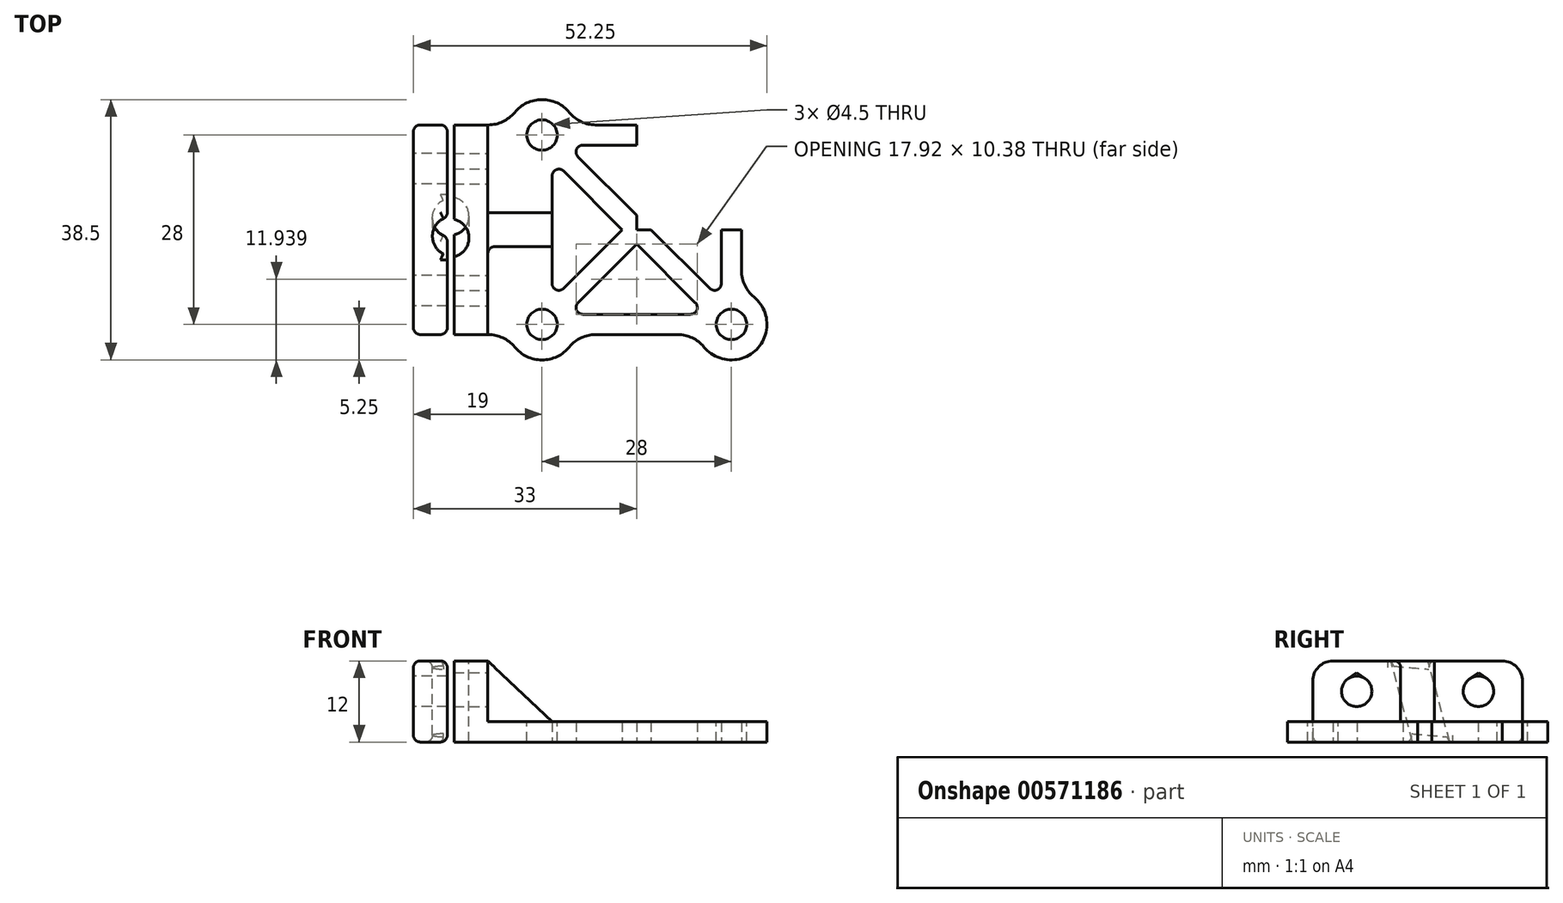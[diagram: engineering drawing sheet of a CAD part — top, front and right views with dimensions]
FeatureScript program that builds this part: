
annotation { "Feature Type Name" : "Feature", "Feature Type Description" : "" }
export const myFeature = defineFeature(function(context is Context, id is Id, definition is map)
    precondition{}
    {
        {
            var Q0;
            Q0=qCreatedBy(makeId("Top.planeOp"),FACE);
            var sketch = newSketch(context, id + "F0", { "sketchPlane" : qUnion([Q0])});
            skCircle(sketch, "E0", {"center": v(-27.5, 0) * mm, "radius": 2.5 * mm});
            skSolve(sketch);
        }
        {
            var Q0;
            Q0=makeQuery(id+"F0.imprint","IMPRINT",FACE,{"disambiguationData":[TD([[makeQuery(id+"F0.imprint","IMPRINT",EDGE,{"derivedFrom":sQuery(id+"F0.wireOp",EDGE,"E0")}),1.0]])]});
            extrude(context, id + "F1", {"entities" : qUnion([Q0]), "endBound" : BoundingType.SYMMETRIC, "depth" : 35 * mm, "offsetDistance" : 25 * mm});
        }
        {
            var Q0;
            Q0=qCreatedBy(makeId("Front.planeOp"),FACE);
            var sketch = newSketch(context, id + "F2", { "sketchPlane" : qUnion([Q0])});
            skLineSegment(sketch, "E1", {"start": v(0, 7.5) * mm, "end": v(-27.5, 7.5) * mm, "construction": true});
            skSolve(sketch);
        }
        {
            var Q0;
            Q0=makeQuery(id+"F1.opExtrude","SWEPT_BODY",BODY,{"disambiguationData":[OSD([sQuery(id+"F0.wireOp",EDGE,"E0")])]});
            var Q1;
            Q1=sQuery(id+"F2.wireOp",EDGE,"E1");
            transform(context, id + "F3", {"entities" : qUnion([Q0]), "transformType" : TransformType.ROTATION, "transformAxis" : qUnion([Q1]), "angle" : 15 * degree, "oppositeDirection" : true, "makeCopy" : false});
        }
        {
            var Q0;
            Q0=qCreatedBy(makeId("Top.planeOp"),FACE);
            var sketch = newSketch(context, id + "F4", { "sketchPlane" : qUnion([Q0])});
            skArc(sketch, "E2", {"start": v(-15.5, -8.97) * mm, "mid": v(-17.71, -17.71) * mm, "end": v(-8.97, -15.5) * mm});
            skCircle(sketch, "E3", {"center": v(-14, -14) * mm, "radius": 2.25 * mm, "construction": true});
            skLineSegment(sketch, "E4", {"start": v(-14, -14) * mm, "end": v(0, -14) * mm, "construction": true});
            skLineSegment(sketch, "E5", {"start": v(0, 0) * mm, "end": v(-14, -14) * mm, "construction": true});
            skLineSegment(sketch, "E6", {"start": v(-14, 0) * mm, "end": v(-14, -14) * mm, "construction": true});
            skLineSegment(sketch, "E7", {"start": v(-8.97, -15.5) * mm, "end": v(0, -15.5) * mm});
            skLineSegment(sketch, "E8", {"start": v(0, -15.5) * mm, "end": v(0, -14) * mm});
            skLineSegment(sketch, "E9", {"start": v(0, -12.5) * mm, "end": v(-7.96, -12.5) * mm});
            skLineSegment(sketch, "E10", {"start": v(-15.5, -8.97) * mm, "end": v(-15.5, 0) * mm});
            skLineSegment(sketch, "E11", {"start": v(-15.5, 0) * mm, "end": v(-14, 0) * mm});
            skLineSegment(sketch, "E12", {"start": v(-10.8, -8.67) * mm, "end": v(-2.12, 0) * mm});
            skLineSegment(sketch, "E13", {"start": v(0, -2.12) * mm, "end": v(-8.67, -10.8) * mm});
            skLineSegment(sketch, "E14", {"start": v(-14, 0) * mm, "end": v(-12.5, 0) * mm});
            skLineSegment(sketch, "E15", {"start": v(-12.5, 0) * mm, "end": v(-12.5, -7.96) * mm});
            skLineSegment(sketch, "E16", {"start": v(0, -12.5) * mm, "end": v(0, -14) * mm});
            skArc(sketch, "E17", {"start": v(-12.5, -7.96) * mm, "mid": v(-11.88, -8.89) * mm, "end": v(-10.8, -8.67) * mm});
            skArc(sketch, "E18", {"start": v(-8.67, -10.8) * mm, "mid": v(-8.89, -11.88) * mm, "end": v(-7.96, -12.5) * mm});
            skLineSegment(sketch, "E19", {"start": v(-2.12, 0) * mm, "end": v(0, 0) * mm});
            skLineSegment(sketch, "E20", {"start": v(0, 0) * mm, "end": v(0, -2.12) * mm});
            skLineSegment(sketch, "E21", {"start": v(-2.12, 0) * mm, "end": v(-1.06, -1.06) * mm, "construction": true});
            skLineSegment(sketch, "E22", {"start": v(-1.06, -1.06) * mm, "end": v(0, -2.12) * mm, "construction": true});
            skSolve(sketch);
        }
        {
            var Q0;
            Q0 = qSketchRegion(id + "F4", true);
            extrude(context, id + "F5", {"entities" : qUnion([Q0]), "depth" : 3 * mm, "offsetDistance" : 25 * mm});
        }
        {
            var Q0;
            Q0=makeQuery(id+"F5.opExtrude","CAP_FACE",FACE,{"disambiguationData":[OSD([sQuery(id+"F4.wireOp",EDGE,"E2"),sQuery(id+"F4.wireOp",EDGE,"E7"),sQuery(id+"F4.wireOp",EDGE,"E8"),sQuery(id+"F4.wireOp",EDGE,"E9"),sQuery(id+"F4.wireOp",EDGE,"E10"),sQuery(id+"F4.wireOp",EDGE,"E11"),sQuery(id+"F4.wireOp",EDGE,"E12"),sQuery(id+"F4.wireOp",EDGE,"Kl6RHnXf-nioG-wzmg-PsDO-Y8z6quR7Twf4"),sQuery(id+"F4.wireOp",EDGE,"E13"),sQuery(id+"F4.wireOp",EDGE,"E14"),sQuery(id+"F4.wireOp",EDGE,"E15"),sQuery(id+"F4.wireOp",EDGE,"vt1vT131-rDiG-MxEs-hZJZ-qJtVu3JIf4gR"),sQuery(id+"F4.wireOp",EDGE,"E16"),sQuery(id+"F4.wireOp",EDGE,"E17"),sQuery(id+"F4.wireOp",EDGE,"E18")])],"isStart":false});
            var sketch = newSketch(context, id + "F6", { "sketchPlane" : qUnion([Q0])});
            skCircle(sketch, "E23", {"center": v(-14, -14) * mm, "radius": 2.25 * mm});
            skSolve(sketch);
        }
        {
            var Q0;
            Q0 = qSketchRegion(id + "F6", true);
            var Q1;
            Q1=makeQuery(id+"F5.opExtrude","CAP_FACE",FACE,{"disambiguationData":[OSD([sQuery(id+"F4.wireOp",EDGE,"E2"),sQuery(id+"F4.wireOp",EDGE,"E7"),sQuery(id+"F4.wireOp",EDGE,"E8"),sQuery(id+"F4.wireOp",EDGE,"E9"),sQuery(id+"F4.wireOp",EDGE,"E10"),sQuery(id+"F4.wireOp",EDGE,"E11"),sQuery(id+"F4.wireOp",EDGE,"E12"),sQuery(id+"F4.wireOp",EDGE,"Kl6RHnXf-nioG-wzmg-PsDO-Y8z6quR7Twf4"),sQuery(id+"F4.wireOp",EDGE,"E13"),sQuery(id+"F4.wireOp",EDGE,"E14"),sQuery(id+"F4.wireOp",EDGE,"E15"),sQuery(id+"F4.wireOp",EDGE,"vt1vT131-rDiG-MxEs-hZJZ-qJtVu3JIf4gR"),sQuery(id+"F4.wireOp",EDGE,"E16"),sQuery(id+"F4.wireOp",EDGE,"E17"),sQuery(id+"F4.wireOp",EDGE,"E18")])],"isStart":true});
            extrude(context, id + "F7", {"entities" : qUnion([Q0]), "operationType" : NewBodyOperationType.REMOVE, "endBound" : BoundingType.UP_TO_SURFACE, "oppositeDirection" : true, "depth" : 25 * mm, "endBoundEntityFace" : qUnion([Q1]), "offsetDistance" : 25 * mm});
        }
        {
            var Q0;
            Q0=makeQuery(id+"F5.opExtrude","SWEPT_BODY",BODY,{"disambiguationData":[OSD([sQuery(id+"F4.wireOp",EDGE,"E2"),sQuery(id+"F4.wireOp",EDGE,"E7"),sQuery(id+"F4.wireOp",EDGE,"E8"),sQuery(id+"F4.wireOp",EDGE,"E9"),sQuery(id+"F4.wireOp",EDGE,"E10"),sQuery(id+"F4.wireOp",EDGE,"E11"),sQuery(id+"F4.wireOp",EDGE,"E12"),sQuery(id+"F4.wireOp",EDGE,"Kl6RHnXf-nioG-wzmg-PsDO-Y8z6quR7Twf4"),sQuery(id+"F4.wireOp",EDGE,"E13"),sQuery(id+"F4.wireOp",EDGE,"E14"),sQuery(id+"F4.wireOp",EDGE,"E15"),sQuery(id+"F4.wireOp",EDGE,"vt1vT131-rDiG-MxEs-hZJZ-qJtVu3JIf4gR"),sQuery(id+"F4.wireOp",EDGE,"E16"),sQuery(id+"F4.wireOp",EDGE,"E17"),sQuery(id+"F4.wireOp",EDGE,"E18")])]});
            var Q1;
            Q1=qCreatedBy(makeId("Right.planeOp"),FACE);
            mirror(context, id + "F8", {"operationType" : NewBodyOperationType.ADD, "entities" : qUnion([Q0]), "mirrorPlane" : qUnion([Q1])});
        }
        {
            var Q0;
            Q0=makeQuery(id+"F5.opExtrude","SWEPT_BODY",BODY,{"disambiguationData":[OSD([sQuery(id+"F4.wireOp",EDGE,"E2"),sQuery(id+"F4.wireOp",EDGE,"E7"),sQuery(id+"F4.wireOp",EDGE,"E8"),sQuery(id+"F4.wireOp",EDGE,"E9"),sQuery(id+"F4.wireOp",EDGE,"E10"),sQuery(id+"F4.wireOp",EDGE,"E11"),sQuery(id+"F4.wireOp",EDGE,"E12"),sQuery(id+"F4.wireOp",EDGE,"Kl6RHnXf-nioG-wzmg-PsDO-Y8z6quR7Twf4"),sQuery(id+"F4.wireOp",EDGE,"E13"),sQuery(id+"F4.wireOp",EDGE,"E14"),sQuery(id+"F4.wireOp",EDGE,"E15"),sQuery(id+"F4.wireOp",EDGE,"vt1vT131-rDiG-MxEs-hZJZ-qJtVu3JIf4gR"),sQuery(id+"F4.wireOp",EDGE,"E16"),sQuery(id+"F4.wireOp",EDGE,"E17"),sQuery(id+"F4.wireOp",EDGE,"E18")])]});
            var Q1;
            Q1=qCreatedBy(makeId("Front.planeOp"),FACE);
            mirror(context, id + "F9", {"operationType" : NewBodyOperationType.ADD, "entities" : qUnion([Q0]), "mirrorPlane" : qUnion([Q1])});
        }
        {
            var Q0;
            Q0=qCreatedBy(makeId("Top.planeOp"),FACE);
            var sketch = newSketch(context, id + "F10", { "sketchPlane" : qUnion([Q0])});
            skLineSegment(sketch, "E24", {"start": v(-22, 0) * mm, "end": v(-22, -15.5) * mm});
            skLineSegment(sketch, "E25", {"start": v(-22, -15.5) * mm, "end": v(-33, -15.5) * mm});
            skLineSegment(sketch, "E26", {"start": v(-33, -15.5) * mm, "end": v(-33, 0) * mm});
            skLineSegment(sketch, "E27.MirrorCS", {"start": v(-22, 0) * mm, "end": v(-22, 15.5) * mm});
            skLineSegment(sketch, "E28.MirrorCS", {"start": v(-22, 15.5) * mm, "end": v(-33, 15.5) * mm});
            skLineSegment(sketch, "E29.MirrorCS", {"start": v(-33, 15.5) * mm, "end": v(-33, 0) * mm});
            skSolve(sketch);
        }
        {
            var Q0;
            Q0 = qSketchRegion(id + "F10", true);
            extrude(context, id + "F11", {"entities" : qUnion([Q0]), "operationType" : NewBodyOperationType.ADD, "depth" : 12 * mm, "offsetDistance" : 25 * mm});
        }
        {
            var Q0;
            Q0=qCreatedBy(makeId("Top.planeOp"),FACE);
            var sketch = newSketch(context, id + "F12", { "sketchPlane" : qUnion([Q0])});
            skLineSegment(sketch, "E30", {"start": v(-15.68, -15.5) * mm, "end": v(-22, -15.5) * mm});
            skLineSegment(sketch, "E31", {"start": v(-14, 0) * mm, "end": v(-14, -11.75) * mm});
            skArc(sketch, "E32", {"start": v(-14, -11.75) * mm, "mid": v(-16.05, -13.08) * mm, "end": v(-15.68, -15.5) * mm});
            skLineSegment(sketch, "E33", {"start": v(-22, 0) * mm, "end": v(-22, -15.5) * mm});
            skLineSegment(sketch, "E34.MirrorCS", {"start": v(-14, 0) * mm, "end": v(-14, 11.75) * mm});
            skArc(sketch, "E35.MirrorCS", {"start": v(-14, 11.75) * mm, "mid": v(-16.05, 13.08) * mm, "end": v(-15.68, 15.5) * mm});
            skLineSegment(sketch, "E36.MirrorCS", {"start": v(-15.68, 15.5) * mm, "end": v(-22, 15.5) * mm});
            skLineSegment(sketch, "E37.MirrorCS", {"start": v(-22, 0) * mm, "end": v(-22, 15.5) * mm});
            skSolve(sketch);
        }
        {
            var Q0;
            Q0 = qSketchRegion(id + "F12", true);
            var Q1;
            {var subQ0=makeQuery(id+"F5.opExtrude","CAP_FACE",FACE,{"disambiguationData":[OSD([sQuery(id+"F4.wireOp",EDGE,"E2"),sQuery(id+"F4.wireOp",EDGE,"E7"),sQuery(id+"F4.wireOp",EDGE,"E8"),sQuery(id+"F4.wireOp",EDGE,"E9"),sQuery(id+"F4.wireOp",EDGE,"E10"),sQuery(id+"F4.wireOp",EDGE,"E11"),sQuery(id+"F4.wireOp",EDGE,"E12"),sQuery(id+"F4.wireOp",EDGE,"E13"),sQuery(id+"F4.wireOp",EDGE,"E14"),sQuery(id+"F4.wireOp",EDGE,"E15"),sQuery(id+"F4.wireOp",EDGE,"E16"),sQuery(id+"F4.wireOp",EDGE,"E17"),sQuery(id+"F4.wireOp",EDGE,"E18"),sQuery(id+"F4.wireOp",EDGE,"E19"),sQuery(id+"F4.wireOp",EDGE,"E20")])],"isStart":false});var subQ1=makeQuery(id+"F8.boolean.opBoolean","MERGE",FACE,{"derivedFrom":[subQ0,makeQuery(id+"F8.opPattern","COPY",FACE,{"derivedFrom":subQ0,"instanceName":"1"})]});Q1=makeQuery(id+"F9.boolean.opBoolean","MERGE",FACE,{"derivedFrom":[subQ1,makeQuery(id+"F9.opPattern","COPY",FACE,{"derivedFrom":subQ1,"instanceName":"1"})]});}
            extrude(context, id + "F13", {"entities" : qUnion([Q0]), "operationType" : NewBodyOperationType.ADD, "endBound" : BoundingType.UP_TO_SURFACE, "depth" : 25 * mm, "endBoundEntityFace" : qUnion([Q1]), "offsetDistance" : 25 * mm});
        }
        {
            var Q0;
            Q0=qCreatedBy(makeId("Front.planeOp"),FACE);
            var sketch = newSketch(context, id + "F14", { "sketchPlane" : qUnion([Q0])});
            skLineSegment(sketch, "E38", {"start": v(-22, 12) * mm, "end": v(-12.5, 3) * mm});
            skLineSegment(sketch, "E39", {"start": v(-22, 3) * mm, "end": v(-22, 12) * mm});
            skLineSegment(sketch, "E40", {"start": v(-12.5, 3) * mm, "end": v(-22, 3) * mm});
            skSolve(sketch);
        }
        {
            var Q0;
            Q0 = qSketchRegion(id + "F14", true);
            var Q1;
            Q1=makeQuery(id+"F13.opExtrude","SWEPT_FACE",FACE,{"disambiguationData":[OSD([sQuery(id+"F12.wireOp",EDGE,"puVTzyak-XMDq-GeyV-AaeZ-wzUpr93Q762x")])]});
            var Q2;
            Q2=makeQuery(id+"F13.opExtrude","SWEPT_FACE",FACE,{"disambiguationData":[OSD([sQuery(id+"F12.wireOp",EDGE,"d726f810-fd56-4b56-9927-8afe40f47e5f0.MirrorCS")])]});
            extrude(context, id + "F15", {"entities" : qUnion([Q0]), "operationType" : NewBodyOperationType.ADD, "endBound" : BoundingType.SYMMETRIC, "depth" : 5 * mm, "endBoundEntityFace" : qUnion([Q1]), "offsetDistance" : 25 * mm, "hasSecondDirection" : true, "secondDirectionBound" : SecondDirectionBoundingType.UP_TO_SURFACE, "secondDirectionOppositeDirection" : true, "secondDirectionDepth" : 25 * mm, "secondDirectionBoundEntityFace" : qUnion([Q2])});
        }
        {
            var Q0;
            Q0=makeQuery(id+"F1.opExtrude","CAP_FACE",FACE,{"disambiguationData":[OSD([sQuery(id+"F0.wireOp",EDGE,"E0")])],"isStart":false});
            var sketch = newSketch(context, id + "F16", { "sketchPlane" : qUnion([Q0])});
            skArc(sketch, "E41", {"start": v(-27, -0.71) * mm, "mid": v(-24.8, 1.94) * mm, "end": v(-27, 4.6) * mm});
            skLineSegment(sketch, "E42.top", {"start": v(-28, -23.06) * mm, "end": v(-27, -23.06) * mm});
            skLineSegment(sketch, "E42.left", {"start": v(-28, -0.71) * mm, "end": v(-28, -23.06) * mm});
            skLineSegment(sketch, "E42.right", {"start": v(-27, -0.71) * mm, "end": v(-27, -23.06) * mm});
            skLineSegment(sketch, "E43.MirrorCS", {"start": v(-28, 4.6) * mm, "end": v(-28, 26.94) * mm});
            skLineSegment(sketch, "E44.MirrorCS", {"start": v(-28, 26.94) * mm, "end": v(-27, 26.94) * mm});
            skLineSegment(sketch, "E45.MirrorCS", {"start": v(-27, 4.6) * mm, "end": v(-27, 26.94) * mm});
            skArc(sketch, "E46.trimOffspring", {"start": v(-28, 4.6) * mm, "mid": v(-30.2, 1.94) * mm, "end": v(-28, -0.71) * mm});
            skSolve(sketch);
        }
        {
            var Q0;
            Q0 = qSketchRegion(id + "F16", true);
            extrude(context, id + "F17", {"entities" : qUnion([Q0]), "operationType" : NewBodyOperationType.REMOVE, "oppositeDirection" : true, "depth" : 50 * mm, "offsetDistance" : 25 * mm});
        }
        {
            var Q0;
            {var subQ33=sQuery(id+"F10.wireOp",EDGE,"E27.MirrorCS");var subQ35=sQuery(id+"F10.wireOp",EDGE,"E25");var subQ36=sQuery(id+"F10.wireOp",EDGE,"E24");Q0=makeQuery(id+"F15.boolean.opBoolean","SPLIT",FACE,{"disambiguationData":[TD([makeQuery(id+"F11.opExtrude","SWEPT_FACE",FACE,{"disambiguationData":[OSD([subQ35])]})])],"derivedFrom":makeQuery(id+"F11.opExtrude","SWEPT_FACE",FACE,{"disambiguationData":[OSD([subQ36,subQ33])]})});}
            var sketch = newSketch(context, id + "F18", { "sketchPlane" : qUnion([Q0])});
            skLineSegment(sketch, "E47", {"start": v(-15.5, 3) * mm, "end": v(-2.5, 12) * mm, "construction": true});
            skLineSegment(sketch, "E48", {"start": v(-15.5, 12) * mm, "end": v(-2.5, 3) * mm, "construction": true});
            skArc(sketch, "E49", {"start": v(-10.3, 9.34) * mm, "mid": v(-9, 5.25) * mm, "end": v(-7.7, 9.34) * mm});
            skLineSegment(sketch, "E50", {"start": v(-10.3, 9.34) * mm, "end": v(-9, 10.25) * mm});
            skLineSegment(sketch, "E51", {"start": v(-9, 10.25) * mm, "end": v(-7.7, 9.34) * mm});
            skLineSegment(sketch, "E52.MirrorCS", {"start": v(9, 10.25) * mm, "end": v(7.7, 9.34) * mm});
            skArc(sketch, "E53.MirrorCS", {"start": v(10.3, 9.34) * mm, "mid": v(9, 5.25) * mm, "end": v(7.7, 9.34) * mm});
            skLineSegment(sketch, "E54.MirrorCS", {"start": v(10.3, 9.34) * mm, "end": v(9, 10.25) * mm});
            skSolve(sketch);
        }
        {
            var Q0;
            Q0 = qSketchRegion(id + "F18", true);
            var Q1;
            Q1=makeQuery(id+"F17.boolean.opBoolean","COPY",FACE,{"derivedFrom":makeQuery(id+"F17.opExtrude","SWEPT_FACE",FACE,{"disambiguationData":[OSD([sQuery(id+"F16.wireOp",EDGE,"E42.right")])]})});
            extrude(context, id + "F19", {"entities" : qUnion([Q0]), "operationType" : NewBodyOperationType.REMOVE, "endBound" : BoundingType.UP_TO_SURFACE, "oppositeDirection" : true, "depth" : 25 * mm, "endBoundEntityFace" : qUnion([Q1]), "offsetDistance" : 25 * mm});
        }
        {
            var Q0;
            Q0=makeQuery(id+"F11.opExtrude","SWEPT_FACE",FACE,{"disambiguationData":[OSD([sQuery(id+"F10.wireOp",EDGE,"E26"),sQuery(id+"F10.wireOp",EDGE,"E29.MirrorCS")])]});
            var sketch = newSketch(context, id + "F20", { "sketchPlane" : qUnion([Q0])});
            skCircle(sketch, "E55", {"center": v(9, 7.5) * mm, "radius": 2.25 * mm});
            skCircle(sketch, "E56.MirrorC", {"center": v(-9, 7.5) * mm, "radius": 2.25 * mm});
            skSolve(sketch);
        }
        {
            var Q0;
            Q0 = qSketchRegion(id + "F20", true);
            var Q1;
            Q1=makeQuery(id+"F17.boolean.opBoolean","COPY",FACE,{"derivedFrom":makeQuery(id+"F17.opExtrude","SWEPT_FACE",FACE,{"disambiguationData":[OSD([sQuery(id+"F16.wireOp",EDGE,"E42.left")])]})});
            extrude(context, id + "F21", {"entities" : qUnion([Q0]), "operationType" : NewBodyOperationType.REMOVE, "endBound" : BoundingType.UP_TO_SURFACE, "oppositeDirection" : true, "depth" : 25 * mm, "endBoundEntityFace" : qUnion([Q1]), "offsetDistance" : 25 * mm});
        }
        {
            var Q0;
            Q0=makeQuery(id+"F9.opPattern","COPY",EDGE,{"derivedFrom":makeQuery(id+"F8.opPattern","COPY",EDGE,{"derivedFrom":makeQuery(id+"F5.opExtrude","SWEPT_EDGE",EDGE,{"disambiguationData":[OSD([sQuery(id+"F4.wireOp",EDGE,"E2"),sQuery(id+"F4.wireOp",EDGE,"E7")])]}),"instanceName":"1"}),"instanceName":"1"});
            var Q1;
            Q1=makeQuery(id+"F9.opPattern","COPY",EDGE,{"derivedFrom":makeQuery(id+"F5.opExtrude","SWEPT_EDGE",EDGE,{"disambiguationData":[OSD([sQuery(id+"F4.wireOp",EDGE,"E2"),sQuery(id+"F4.wireOp",EDGE,"E7")])]}),"instanceName":"1"});
            var Q2;
            Q2=makeQuery(id+"F9.opPattern","COPY",EDGE,{"derivedFrom":makeQuery(id+"F5.opExtrude","SWEPT_EDGE",EDGE,{"disambiguationData":[OSD([sQuery(id+"F4.wireOp",EDGE,"E2"),sQuery(id+"F4.wireOp",EDGE,"E10")])]}),"instanceName":"1"});
            var Q3;
            Q3=makeQuery(id+"F5.opExtrude","SWEPT_EDGE",EDGE,{"disambiguationData":[OSD([sQuery(id+"F4.wireOp",EDGE,"E2"),sQuery(id+"F4.wireOp",EDGE,"E10")])]});
            var Q4;
            Q4=makeQuery(id+"F5.opExtrude","SWEPT_EDGE",EDGE,{"disambiguationData":[OSD([sQuery(id+"F4.wireOp",EDGE,"E2"),sQuery(id+"F4.wireOp",EDGE,"E7")])]});
            var Q5;
            Q5=makeQuery(id+"F8.opPattern","COPY",EDGE,{"derivedFrom":makeQuery(id+"F5.opExtrude","SWEPT_EDGE",EDGE,{"disambiguationData":[OSD([sQuery(id+"F4.wireOp",EDGE,"E2"),sQuery(id+"F4.wireOp",EDGE,"E7")])]}),"instanceName":"1"});
            var Q6;
            Q6=makeQuery(id+"F8.opPattern","COPY",EDGE,{"derivedFrom":makeQuery(id+"F5.opExtrude","SWEPT_EDGE",EDGE,{"disambiguationData":[OSD([sQuery(id+"F4.wireOp",EDGE,"E2"),sQuery(id+"F4.wireOp",EDGE,"E10")])]}),"instanceName":"1"});
            var Q7;
            Q7=makeQuery(id+"F9.opPattern","COPY",EDGE,{"derivedFrom":makeQuery(id+"F8.opPattern","COPY",EDGE,{"derivedFrom":makeQuery(id+"F5.opExtrude","SWEPT_EDGE",EDGE,{"disambiguationData":[OSD([sQuery(id+"F4.wireOp",EDGE,"E2"),sQuery(id+"F4.wireOp",EDGE,"E10")])]}),"instanceName":"1"}),"instanceName":"1"});
            var Q8;
            Q8=makeQuery(id+"F13.boolean.opBoolean","INTERSECT",EDGE,{"derivedFrom":[makeQuery(id+"F5.opExtrude","SWEPT_FACE",FACE,{"disambiguationData":[OSD([sQuery(id+"F4.wireOp",EDGE,"E2")])]}),makeQuery(id+"F13.opExtrude","SWEPT_FACE",FACE,{"disambiguationData":[OSD([sQuery(id+"F12.wireOp",EDGE,"E30")])]})]});
            var Q9;
            Q9=makeQuery(id+"F13.boolean.opBoolean","INTERSECT",EDGE,{"derivedFrom":[makeQuery(id+"F9.opPattern","COPY",FACE,{"derivedFrom":makeQuery(id+"F5.opExtrude","SWEPT_FACE",FACE,{"disambiguationData":[OSD([sQuery(id+"F4.wireOp",EDGE,"E2")])]}),"instanceName":"1"}),makeQuery(id+"F13.opExtrude","SWEPT_FACE",FACE,{"disambiguationData":[OSD([sQuery(id+"F12.wireOp",EDGE,"E36.MirrorCS")])]})]});
            fillet(context, id + "F22", {"entities" : qUnion([Q0, Q1, Q2, Q3, Q4, Q5, Q6, Q7, Q8, Q9]), "radius" : 5 * mm, "tangentPropagation" : true, "allowEdgeOverflow" : false});
        }
        {
            var Q0;
            Q0=makeQuery(id+"F15.opExtrude","CAP_EDGE",EDGE,{"disambiguationData":[OSD([sQuery(id+"F14.wireOp",EDGE,"E39")])],"isStart":false});
            var Q1;
            Q1=makeQuery(id+"F15.opExtrude","CAP_EDGE",EDGE,{"disambiguationData":[OSD([sQuery(id+"F14.wireOp",EDGE,"E40")])],"isStart":false});
            var Q2;
            {var subQ4=sQuery(id+"F12.wireOp",EDGE,"E37.MirrorCS");var subQ5=sQuery(id+"F12.wireOp",EDGE,"E33");Q2=makeQuery(id+"F15.boolean.opBoolean","SPLIT",EDGE,{"disambiguationData":[TD([makeQuery(id+"F11.opExtrude","SWEPT_FACE",FACE,{"disambiguationData":[OSD([sQuery(id+"F10.wireOp",EDGE,"E25")])]})])],"derivedFrom":makeQuery(id+"F13.opExtrude","CAP_EDGE",EDGE,{"disambiguationData":[OSD([subQ5,subQ4])],"isStart":false})});}
            var Q3;
            Q3=makeQuery(id+"F15.opExtrude","CAP_EDGE",EDGE,{"disambiguationData":[OSD([sQuery(id+"F14.wireOp",EDGE,"E40")])],"isStart":true});
            var Q4;
            Q4=makeQuery(id+"F15.opExtrude","CAP_EDGE",EDGE,{"disambiguationData":[OSD([sQuery(id+"F14.wireOp",EDGE,"E39")])],"isStart":true});
            var Q5;
            {var subQ3=sQuery(id+"F12.wireOp",EDGE,"E37.MirrorCS");var subQ5=sQuery(id+"F12.wireOp",EDGE,"E33");Q5=makeQuery(id+"F15.boolean.opBoolean","SPLIT",EDGE,{"disambiguationData":[TD([makeQuery(id+"F11.opExtrude","SWEPT_FACE",FACE,{"disambiguationData":[OSD([sQuery(id+"F10.wireOp",EDGE,"E28.MirrorCS")])]})])],"derivedFrom":makeQuery(id+"F13.opExtrude","CAP_EDGE",EDGE,{"disambiguationData":[OSD([subQ5,subQ3])],"isStart":false})});}
            fillet(context, id + "F23", {"entities" : qUnion([Q0, Q1, Q2, Q3, Q4, Q5]), "radius" : 1 * mm, "tangentPropagation" : true, "allowEdgeOverflow" : false});
        }
        {
            var Q0;
            {var subQ0=sQuery(id+"F10.wireOp",EDGE,"E25");Q0=makeQuery(id+"F17.boolean.opBoolean","SPLIT",EDGE,{"disambiguationData":[TD([makeQuery(id+"F17.opExtrude","SWEPT_FACE",FACE,{"disambiguationData":[OSD([sQuery(id+"F16.wireOp",EDGE,"E42.right")])]})])],"derivedFrom":makeQuery(id+"F11.opExtrude","CAP_EDGE",EDGE,{"disambiguationData":[OSD([subQ0])],"isStart":false})});}
            var Q1;
            {var subQ2=sQuery(id+"F10.wireOp",EDGE,"E25");Q1=makeQuery(id+"F17.boolean.opBoolean","SPLIT",EDGE,{"disambiguationData":[TD([makeQuery(id+"F17.opExtrude","SWEPT_FACE",FACE,{"disambiguationData":[OSD([sQuery(id+"F16.wireOp",EDGE,"E42.left")])]})])],"derivedFrom":makeQuery(id+"F11.opExtrude","CAP_EDGE",EDGE,{"disambiguationData":[OSD([subQ2])],"isStart":false})});}
            var Q2;
            {var subQ0=sQuery(id+"F10.wireOp",EDGE,"E28.MirrorCS");Q2=makeQuery(id+"F17.boolean.opBoolean","SPLIT",EDGE,{"disambiguationData":[TD([makeQuery(id+"F17.opExtrude","SWEPT_FACE",FACE,{"disambiguationData":[OSD([sQuery(id+"F16.wireOp",EDGE,"E45.MirrorCS")])]})])],"derivedFrom":makeQuery(id+"F11.opExtrude","CAP_EDGE",EDGE,{"disambiguationData":[OSD([subQ0])],"isStart":false})});}
            var Q3;
            {var subQ0=sQuery(id+"F10.wireOp",EDGE,"E28.MirrorCS");Q3=makeQuery(id+"F17.boolean.opBoolean","SPLIT",EDGE,{"disambiguationData":[TD([makeQuery(id+"F17.opExtrude","SWEPT_FACE",FACE,{"disambiguationData":[OSD([sQuery(id+"F16.wireOp",EDGE,"E43.MirrorCS")])]})])],"derivedFrom":makeQuery(id+"F11.opExtrude","CAP_EDGE",EDGE,{"disambiguationData":[OSD([subQ0])],"isStart":false})});}
            fillet(context, id + "F24", {"entities" : qUnion([Q0, Q1, Q2, Q3]), "radius" : 3 * mm, "tangentPropagation" : true, "allowEdgeOverflow" : false});
        }
        {
            var Q0;
            Q0=makeQuery(id+"F5.opExtrude","CAP_EDGE",EDGE,{"disambiguationData":[OSD([sQuery(id+"F4.wireOp",EDGE,"E12")])],"isStart":false});
            var Q1;
            Q1=makeQuery(id+"F9.opPattern","COPY",EDGE,{"derivedFrom":makeQuery(id+"F5.opExtrude","CAP_EDGE",EDGE,{"disambiguationData":[OSD([sQuery(id+"F4.wireOp",EDGE,"E12")])],"isStart":false}),"instanceName":"1"});
            var Q2;
            Q2=makeQuery(id+"F9.opPattern","COPY",EDGE,{"derivedFrom":makeQuery(id+"F5.opExtrude","CAP_EDGE",EDGE,{"disambiguationData":[OSD([sQuery(id+"F4.wireOp",EDGE,"E13")])],"isStart":false}),"instanceName":"1"});
            var Q3;
            Q3=makeQuery(id+"F9.opPattern","COPY",EDGE,{"derivedFrom":makeQuery(id+"F8.opPattern","COPY",EDGE,{"derivedFrom":makeQuery(id+"F5.opExtrude","CAP_EDGE",EDGE,{"disambiguationData":[OSD([sQuery(id+"F4.wireOp",EDGE,"E12")])],"isStart":false}),"instanceName":"1"}),"instanceName":"1"});
            var Q4;
            Q4=makeQuery(id+"F8.opPattern","COPY",EDGE,{"derivedFrom":makeQuery(id+"F5.opExtrude","CAP_EDGE",EDGE,{"disambiguationData":[OSD([sQuery(id+"F4.wireOp",EDGE,"E13")])],"isStart":false}),"instanceName":"1"});
            var Q5;
            {var subQ0=makeQuery(id+"F8.opPattern","COPY",EDGE,{"derivedFrom":makeQuery(id+"F5.opExtrude","CAP_EDGE",EDGE,{"disambiguationData":[OSD([sQuery(id+"F4.wireOp",EDGE,"E10")])],"isStart":false}),"instanceName":"1"});Q5=makeQuery(id+"F9.boolean.opBoolean","MERGE",EDGE,{"derivedFrom":[subQ0,makeQuery(id+"F9.opPattern","COPY",EDGE,{"derivedFrom":subQ0,"instanceName":"1"})]});}
            var Q6;
            Q6=makeQuery(id+"F11.opExtrude","CAP_EDGE",EDGE,{"disambiguationData":[OSD([sQuery(id+"F10.wireOp",EDGE,"E26"),sQuery(id+"F10.wireOp",EDGE,"E29.MirrorCS")])],"isStart":false});
            var Q7;
            Q7=makeQuery(id+"F8.opPattern","COPY",EDGE,{"derivedFrom":makeQuery(id+"F5.opExtrude","CAP_EDGE",EDGE,{"disambiguationData":[OSD([sQuery(id+"F4.wireOp",EDGE,"E2")])],"isStart":true}),"instanceName":"1"});
            var Q8;
            Q8=makeQuery(id+"F5.opExtrude","CAP_EDGE",EDGE,{"disambiguationData":[OSD([sQuery(id+"F4.wireOp",EDGE,"E13")])],"isStart":true});
            var Q9;
            Q9=makeQuery(id+"F9.opPattern","COPY",EDGE,{"derivedFrom":makeQuery(id+"F8.opPattern","COPY",EDGE,{"derivedFrom":makeQuery(id+"F5.opExtrude","CAP_EDGE",EDGE,{"disambiguationData":[OSD([sQuery(id+"F4.wireOp",EDGE,"E12")])],"isStart":true}),"instanceName":"1"}),"instanceName":"1"});
            var Q10;
            {var subQ0=makeQuery(id+"F5.opExtrude","CAP_EDGE",EDGE,{"disambiguationData":[OSD([sQuery(id+"F4.wireOp",EDGE,"E9")])],"isStart":true});Q10=makeQuery(id+"F9.opPattern","COPY",EDGE,{"derivedFrom":makeQuery(id+"F8.boolean.opBoolean","MERGE",EDGE,{"derivedFrom":[subQ0,makeQuery(id+"F8.opPattern","COPY",EDGE,{"derivedFrom":subQ0,"instanceName":"1"})]}),"instanceName":"1"});}
            var Q11;
            Q11=makeQuery(id+"F9.opPattern","COPY",EDGE,{"derivedFrom":makeQuery(id+"F5.opExtrude","CAP_EDGE",EDGE,{"disambiguationData":[OSD([sQuery(id+"F4.wireOp",EDGE,"E17")])],"isStart":true}),"instanceName":"1"});
            var Q12;
            {var subQ0=makeQuery(id+"F5.opExtrude","CAP_FACE",FACE,{"disambiguationData":[OSD([sQuery(id+"F4.wireOp",EDGE,"E2"),sQuery(id+"F4.wireOp",EDGE,"E7"),sQuery(id+"F4.wireOp",EDGE,"E8"),sQuery(id+"F4.wireOp",EDGE,"E9"),sQuery(id+"F4.wireOp",EDGE,"E10"),sQuery(id+"F4.wireOp",EDGE,"E11"),sQuery(id+"F4.wireOp",EDGE,"E12"),sQuery(id+"F4.wireOp",EDGE,"E13"),sQuery(id+"F4.wireOp",EDGE,"E14"),sQuery(id+"F4.wireOp",EDGE,"E15"),sQuery(id+"F4.wireOp",EDGE,"E16"),sQuery(id+"F4.wireOp",EDGE,"E17"),sQuery(id+"F4.wireOp",EDGE,"E18"),sQuery(id+"F4.wireOp",EDGE,"E19"),sQuery(id+"F4.wireOp",EDGE,"E20")])],"isStart":true});var subQ1=makeQuery(id+"F8.boolean.opBoolean","MERGE",FACE,{"derivedFrom":[subQ0,makeQuery(id+"F8.opPattern","COPY",FACE,{"derivedFrom":subQ0,"instanceName":"1"})]});Q12=makeQuery(id+"F17.boolean.opBoolean","INTERSECT",EDGE,{"derivedFrom":[makeQuery(id+"F13.boolean.opBoolean","MERGE",FACE,{"derivedFrom":[makeQuery(id+"F9.boolean.opBoolean","MERGE",FACE,{"derivedFrom":[subQ1,makeQuery(id+"F9.opPattern","COPY",FACE,{"derivedFrom":subQ1,"instanceName":"1"})]}),makeQuery(id+"F11.opExtrude","CAP_FACE",FACE,{"disambiguationData":[OSD([sQuery(id+"F10.wireOp",EDGE,"E24"),sQuery(id+"F10.wireOp",EDGE,"E25"),sQuery(id+"F10.wireOp",EDGE,"E26"),sQuery(id+"F10.wireOp",EDGE,"E27.MirrorCS"),sQuery(id+"F10.wireOp",EDGE,"E28.MirrorCS"),sQuery(id+"F10.wireOp",EDGE,"E29.MirrorCS")])],"isStart":true}),makeQuery(id+"F13.opExtrude","CAP_FACE",FACE,{"disambiguationData":[OSD([sQuery(id+"F12.wireOp",EDGE,"E30"),sQuery(id+"F12.wireOp",EDGE,"E31"),sQuery(id+"F12.wireOp",EDGE,"E32"),sQuery(id+"F12.wireOp",EDGE,"E33"),sQuery(id+"F12.wireOp",EDGE,"E34.MirrorCS"),sQuery(id+"F12.wireOp",EDGE,"E35.MirrorCS"),sQuery(id+"F12.wireOp",EDGE,"E36.MirrorCS"),sQuery(id+"F12.wireOp",EDGE,"E37.MirrorCS")])],"isStart":true})]}),makeQuery(id+"F17.opExtrude","SWEPT_FACE",FACE,{"disambiguationData":[OSD([sQuery(id+"F16.wireOp",EDGE,"E45.MirrorCS")])]})]});}
            var Q13;
            {var subQ0=makeQuery(id+"F5.opExtrude","CAP_FACE",FACE,{"disambiguationData":[OSD([sQuery(id+"F4.wireOp",EDGE,"E2"),sQuery(id+"F4.wireOp",EDGE,"E7"),sQuery(id+"F4.wireOp",EDGE,"E8"),sQuery(id+"F4.wireOp",EDGE,"E9"),sQuery(id+"F4.wireOp",EDGE,"E10"),sQuery(id+"F4.wireOp",EDGE,"E11"),sQuery(id+"F4.wireOp",EDGE,"E12"),sQuery(id+"F4.wireOp",EDGE,"E13"),sQuery(id+"F4.wireOp",EDGE,"E14"),sQuery(id+"F4.wireOp",EDGE,"E15"),sQuery(id+"F4.wireOp",EDGE,"E16"),sQuery(id+"F4.wireOp",EDGE,"E17"),sQuery(id+"F4.wireOp",EDGE,"E18"),sQuery(id+"F4.wireOp",EDGE,"E19"),sQuery(id+"F4.wireOp",EDGE,"E20")])],"isStart":true});var subQ1=makeQuery(id+"F8.boolean.opBoolean","MERGE",FACE,{"derivedFrom":[subQ0,makeQuery(id+"F8.opPattern","COPY",FACE,{"derivedFrom":subQ0,"instanceName":"1"})]});Q13=makeQuery(id+"F17.boolean.opBoolean","INTERSECT",EDGE,{"derivedFrom":[makeQuery(id+"F13.boolean.opBoolean","MERGE",FACE,{"derivedFrom":[makeQuery(id+"F9.boolean.opBoolean","MERGE",FACE,{"derivedFrom":[subQ1,makeQuery(id+"F9.opPattern","COPY",FACE,{"derivedFrom":subQ1,"instanceName":"1"})]}),makeQuery(id+"F11.opExtrude","CAP_FACE",FACE,{"disambiguationData":[OSD([sQuery(id+"F10.wireOp",EDGE,"E24"),sQuery(id+"F10.wireOp",EDGE,"E25"),sQuery(id+"F10.wireOp",EDGE,"E26"),sQuery(id+"F10.wireOp",EDGE,"E27.MirrorCS"),sQuery(id+"F10.wireOp",EDGE,"E28.MirrorCS"),sQuery(id+"F10.wireOp",EDGE,"E29.MirrorCS")])],"isStart":true}),makeQuery(id+"F13.opExtrude","CAP_FACE",FACE,{"disambiguationData":[OSD([sQuery(id+"F12.wireOp",EDGE,"E30"),sQuery(id+"F12.wireOp",EDGE,"E31"),sQuery(id+"F12.wireOp",EDGE,"E32"),sQuery(id+"F12.wireOp",EDGE,"E33"),sQuery(id+"F12.wireOp",EDGE,"E34.MirrorCS"),sQuery(id+"F12.wireOp",EDGE,"E35.MirrorCS"),sQuery(id+"F12.wireOp",EDGE,"E36.MirrorCS"),sQuery(id+"F12.wireOp",EDGE,"E37.MirrorCS")])],"isStart":true})]}),makeQuery(id+"F17.opExtrude","SWEPT_FACE",FACE,{"disambiguationData":[OSD([sQuery(id+"F16.wireOp",EDGE,"E41")])]})]});}
            var Q14;
            {var subQ0=makeQuery(id+"F5.opExtrude","CAP_FACE",FACE,{"disambiguationData":[OSD([sQuery(id+"F4.wireOp",EDGE,"E2"),sQuery(id+"F4.wireOp",EDGE,"E7"),sQuery(id+"F4.wireOp",EDGE,"E8"),sQuery(id+"F4.wireOp",EDGE,"E9"),sQuery(id+"F4.wireOp",EDGE,"E10"),sQuery(id+"F4.wireOp",EDGE,"E11"),sQuery(id+"F4.wireOp",EDGE,"E12"),sQuery(id+"F4.wireOp",EDGE,"E13"),sQuery(id+"F4.wireOp",EDGE,"E14"),sQuery(id+"F4.wireOp",EDGE,"E15"),sQuery(id+"F4.wireOp",EDGE,"E16"),sQuery(id+"F4.wireOp",EDGE,"E17"),sQuery(id+"F4.wireOp",EDGE,"E18"),sQuery(id+"F4.wireOp",EDGE,"E19"),sQuery(id+"F4.wireOp",EDGE,"E20")])],"isStart":true});var subQ1=makeQuery(id+"F8.boolean.opBoolean","MERGE",FACE,{"derivedFrom":[subQ0,makeQuery(id+"F8.opPattern","COPY",FACE,{"derivedFrom":subQ0,"instanceName":"1"})]});Q14=makeQuery(id+"F17.boolean.opBoolean","INTERSECT",EDGE,{"derivedFrom":[makeQuery(id+"F13.boolean.opBoolean","MERGE",FACE,{"derivedFrom":[makeQuery(id+"F9.boolean.opBoolean","MERGE",FACE,{"derivedFrom":[subQ1,makeQuery(id+"F9.opPattern","COPY",FACE,{"derivedFrom":subQ1,"instanceName":"1"})]}),makeQuery(id+"F11.opExtrude","CAP_FACE",FACE,{"disambiguationData":[OSD([sQuery(id+"F10.wireOp",EDGE,"E24"),sQuery(id+"F10.wireOp",EDGE,"E25"),sQuery(id+"F10.wireOp",EDGE,"E26"),sQuery(id+"F10.wireOp",EDGE,"E27.MirrorCS"),sQuery(id+"F10.wireOp",EDGE,"E28.MirrorCS"),sQuery(id+"F10.wireOp",EDGE,"E29.MirrorCS")])],"isStart":true}),makeQuery(id+"F13.opExtrude","CAP_FACE",FACE,{"disambiguationData":[OSD([sQuery(id+"F12.wireOp",EDGE,"E30"),sQuery(id+"F12.wireOp",EDGE,"E31"),sQuery(id+"F12.wireOp",EDGE,"E32"),sQuery(id+"F12.wireOp",EDGE,"E33"),sQuery(id+"F12.wireOp",EDGE,"E34.MirrorCS"),sQuery(id+"F12.wireOp",EDGE,"E35.MirrorCS"),sQuery(id+"F12.wireOp",EDGE,"E36.MirrorCS"),sQuery(id+"F12.wireOp",EDGE,"E37.MirrorCS")])],"isStart":true})]}),makeQuery(id+"F17.opExtrude","SWEPT_FACE",FACE,{"disambiguationData":[OSD([sQuery(id+"F16.wireOp",EDGE,"E42.right")])]})]});}
            var Q15;
            {var subQ0=makeQuery(id+"F5.opExtrude","CAP_FACE",FACE,{"disambiguationData":[OSD([sQuery(id+"F4.wireOp",EDGE,"E2"),sQuery(id+"F4.wireOp",EDGE,"E7"),sQuery(id+"F4.wireOp",EDGE,"E8"),sQuery(id+"F4.wireOp",EDGE,"E9"),sQuery(id+"F4.wireOp",EDGE,"E10"),sQuery(id+"F4.wireOp",EDGE,"E11"),sQuery(id+"F4.wireOp",EDGE,"E12"),sQuery(id+"F4.wireOp",EDGE,"E13"),sQuery(id+"F4.wireOp",EDGE,"E14"),sQuery(id+"F4.wireOp",EDGE,"E15"),sQuery(id+"F4.wireOp",EDGE,"E16"),sQuery(id+"F4.wireOp",EDGE,"E17"),sQuery(id+"F4.wireOp",EDGE,"E18"),sQuery(id+"F4.wireOp",EDGE,"E19"),sQuery(id+"F4.wireOp",EDGE,"E20")])],"isStart":true});var subQ1=makeQuery(id+"F8.boolean.opBoolean","MERGE",FACE,{"derivedFrom":[subQ0,makeQuery(id+"F8.opPattern","COPY",FACE,{"derivedFrom":subQ0,"instanceName":"1"})]});Q15=makeQuery(id+"F17.boolean.opBoolean","INTERSECT",EDGE,{"derivedFrom":[makeQuery(id+"F13.boolean.opBoolean","MERGE",FACE,{"derivedFrom":[makeQuery(id+"F9.boolean.opBoolean","MERGE",FACE,{"derivedFrom":[subQ1,makeQuery(id+"F9.opPattern","COPY",FACE,{"derivedFrom":subQ1,"instanceName":"1"})]}),makeQuery(id+"F11.opExtrude","CAP_FACE",FACE,{"disambiguationData":[OSD([sQuery(id+"F10.wireOp",EDGE,"E24"),sQuery(id+"F10.wireOp",EDGE,"E25"),sQuery(id+"F10.wireOp",EDGE,"E26"),sQuery(id+"F10.wireOp",EDGE,"E27.MirrorCS"),sQuery(id+"F10.wireOp",EDGE,"E28.MirrorCS"),sQuery(id+"F10.wireOp",EDGE,"E29.MirrorCS")])],"isStart":true}),makeQuery(id+"F13.opExtrude","CAP_FACE",FACE,{"disambiguationData":[OSD([sQuery(id+"F12.wireOp",EDGE,"E30"),sQuery(id+"F12.wireOp",EDGE,"E31"),sQuery(id+"F12.wireOp",EDGE,"E32"),sQuery(id+"F12.wireOp",EDGE,"E33"),sQuery(id+"F12.wireOp",EDGE,"E34.MirrorCS"),sQuery(id+"F12.wireOp",EDGE,"E35.MirrorCS"),sQuery(id+"F12.wireOp",EDGE,"E36.MirrorCS"),sQuery(id+"F12.wireOp",EDGE,"E37.MirrorCS")])],"isStart":true})]}),makeQuery(id+"F17.opExtrude","SWEPT_FACE",FACE,{"disambiguationData":[OSD([sQuery(id+"F16.wireOp",EDGE,"E42.left")])]})]});}
            var Q16;
            {var subQ0=makeQuery(id+"F5.opExtrude","CAP_FACE",FACE,{"disambiguationData":[OSD([sQuery(id+"F4.wireOp",EDGE,"E2"),sQuery(id+"F4.wireOp",EDGE,"E7"),sQuery(id+"F4.wireOp",EDGE,"E8"),sQuery(id+"F4.wireOp",EDGE,"E9"),sQuery(id+"F4.wireOp",EDGE,"E10"),sQuery(id+"F4.wireOp",EDGE,"E11"),sQuery(id+"F4.wireOp",EDGE,"E12"),sQuery(id+"F4.wireOp",EDGE,"E13"),sQuery(id+"F4.wireOp",EDGE,"E14"),sQuery(id+"F4.wireOp",EDGE,"E15"),sQuery(id+"F4.wireOp",EDGE,"E16"),sQuery(id+"F4.wireOp",EDGE,"E17"),sQuery(id+"F4.wireOp",EDGE,"E18"),sQuery(id+"F4.wireOp",EDGE,"E19"),sQuery(id+"F4.wireOp",EDGE,"E20")])],"isStart":true});var subQ1=makeQuery(id+"F8.boolean.opBoolean","MERGE",FACE,{"derivedFrom":[subQ0,makeQuery(id+"F8.opPattern","COPY",FACE,{"derivedFrom":subQ0,"instanceName":"1"})]});Q16=makeQuery(id+"F17.boolean.opBoolean","INTERSECT",EDGE,{"derivedFrom":[makeQuery(id+"F13.boolean.opBoolean","MERGE",FACE,{"derivedFrom":[makeQuery(id+"F9.boolean.opBoolean","MERGE",FACE,{"derivedFrom":[subQ1,makeQuery(id+"F9.opPattern","COPY",FACE,{"derivedFrom":subQ1,"instanceName":"1"})]}),makeQuery(id+"F11.opExtrude","CAP_FACE",FACE,{"disambiguationData":[OSD([sQuery(id+"F10.wireOp",EDGE,"E24"),sQuery(id+"F10.wireOp",EDGE,"E25"),sQuery(id+"F10.wireOp",EDGE,"E26"),sQuery(id+"F10.wireOp",EDGE,"E27.MirrorCS"),sQuery(id+"F10.wireOp",EDGE,"E28.MirrorCS"),sQuery(id+"F10.wireOp",EDGE,"E29.MirrorCS")])],"isStart":true}),makeQuery(id+"F13.opExtrude","CAP_FACE",FACE,{"disambiguationData":[OSD([sQuery(id+"F12.wireOp",EDGE,"E30"),sQuery(id+"F12.wireOp",EDGE,"E31"),sQuery(id+"F12.wireOp",EDGE,"E32"),sQuery(id+"F12.wireOp",EDGE,"E33"),sQuery(id+"F12.wireOp",EDGE,"E34.MirrorCS"),sQuery(id+"F12.wireOp",EDGE,"E35.MirrorCS"),sQuery(id+"F12.wireOp",EDGE,"E36.MirrorCS"),sQuery(id+"F12.wireOp",EDGE,"E37.MirrorCS")])],"isStart":true})]}),makeQuery(id+"F17.opExtrude","SWEPT_FACE",FACE,{"disambiguationData":[OSD([sQuery(id+"F16.wireOp",EDGE,"E43.MirrorCS")])]})]});}
            var Q17;
            Q17=makeQuery(id+"F11.opExtrude","CAP_EDGE",EDGE,{"disambiguationData":[OSD([sQuery(id+"F10.wireOp",EDGE,"E26"),sQuery(id+"F10.wireOp",EDGE,"E29.MirrorCS")])],"isStart":true});
            var Q18;
            {var subQ0=makeQuery(id+"F5.opExtrude","CAP_FACE",FACE,{"disambiguationData":[OSD([sQuery(id+"F4.wireOp",EDGE,"E2"),sQuery(id+"F4.wireOp",EDGE,"E7"),sQuery(id+"F4.wireOp",EDGE,"E8"),sQuery(id+"F4.wireOp",EDGE,"E9"),sQuery(id+"F4.wireOp",EDGE,"E10"),sQuery(id+"F4.wireOp",EDGE,"E11"),sQuery(id+"F4.wireOp",EDGE,"E12"),sQuery(id+"F4.wireOp",EDGE,"E13"),sQuery(id+"F4.wireOp",EDGE,"E14"),sQuery(id+"F4.wireOp",EDGE,"E15"),sQuery(id+"F4.wireOp",EDGE,"E16"),sQuery(id+"F4.wireOp",EDGE,"E17"),sQuery(id+"F4.wireOp",EDGE,"E18"),sQuery(id+"F4.wireOp",EDGE,"E19"),sQuery(id+"F4.wireOp",EDGE,"E20")])],"isStart":true});var subQ1=makeQuery(id+"F8.boolean.opBoolean","MERGE",FACE,{"derivedFrom":[subQ0,makeQuery(id+"F8.opPattern","COPY",FACE,{"derivedFrom":subQ0,"instanceName":"1"})]});Q18=makeQuery(id+"F17.boolean.opBoolean","INTERSECT",EDGE,{"derivedFrom":[makeQuery(id+"F13.boolean.opBoolean","MERGE",FACE,{"derivedFrom":[makeQuery(id+"F9.boolean.opBoolean","MERGE",FACE,{"derivedFrom":[subQ1,makeQuery(id+"F9.opPattern","COPY",FACE,{"derivedFrom":subQ1,"instanceName":"1"})]}),makeQuery(id+"F11.opExtrude","CAP_FACE",FACE,{"disambiguationData":[OSD([sQuery(id+"F10.wireOp",EDGE,"E24"),sQuery(id+"F10.wireOp",EDGE,"E25"),sQuery(id+"F10.wireOp",EDGE,"E26"),sQuery(id+"F10.wireOp",EDGE,"E27.MirrorCS"),sQuery(id+"F10.wireOp",EDGE,"E28.MirrorCS"),sQuery(id+"F10.wireOp",EDGE,"E29.MirrorCS")])],"isStart":true}),makeQuery(id+"F13.opExtrude","CAP_FACE",FACE,{"disambiguationData":[OSD([sQuery(id+"F12.wireOp",EDGE,"E30"),sQuery(id+"F12.wireOp",EDGE,"E31"),sQuery(id+"F12.wireOp",EDGE,"E32"),sQuery(id+"F12.wireOp",EDGE,"E33"),sQuery(id+"F12.wireOp",EDGE,"E34.MirrorCS"),sQuery(id+"F12.wireOp",EDGE,"E35.MirrorCS"),sQuery(id+"F12.wireOp",EDGE,"E36.MirrorCS"),sQuery(id+"F12.wireOp",EDGE,"E37.MirrorCS")])],"isStart":true})]}),makeQuery(id+"F17.opExtrude","SWEPT_FACE",FACE,{"disambiguationData":[OSD([sQuery(id+"F16.wireOp",EDGE,"E46.trimOffspring")])]})]});}
            var Q19;
            {var subQ3=sQuery(id+"F10.wireOp",EDGE,"E28.MirrorCS");var subQ6=sQuery(id+"F12.wireOp",EDGE,"E36.MirrorCS");Q19=makeQuery(id+"F17.boolean.opBoolean","SPLIT",EDGE,{"disambiguationData":[TD([makeQuery(id+"F17.opExtrude","SWEPT_FACE",FACE,{"disambiguationData":[OSD([sQuery(id+"F16.wireOp",EDGE,"E43.MirrorCS")])]})])],"derivedFrom":makeQuery(id+"F13.boolean.opBoolean","MERGE",EDGE,{"derivedFrom":[makeQuery(id+"F11.opExtrude","CAP_EDGE",EDGE,{"disambiguationData":[OSD([subQ3])],"isStart":true}),makeQuery(id+"F13.opExtrude","CAP_EDGE",EDGE,{"disambiguationData":[OSD([subQ6])],"isStart":true})]})});}
            var Q20;
            {var subQ5=sQuery(id+"F10.wireOp",EDGE,"E25");var subQ6=sQuery(id+"F12.wireOp",EDGE,"E30");Q20=makeQuery(id+"F17.boolean.opBoolean","SPLIT",EDGE,{"disambiguationData":[TD([makeQuery(id+"F17.opExtrude","SWEPT_FACE",FACE,{"disambiguationData":[OSD([sQuery(id+"F16.wireOp",EDGE,"E42.left")])]})])],"derivedFrom":makeQuery(id+"F13.boolean.opBoolean","MERGE",EDGE,{"derivedFrom":[makeQuery(id+"F11.opExtrude","CAP_EDGE",EDGE,{"disambiguationData":[OSD([subQ5])],"isStart":true}),makeQuery(id+"F13.opExtrude","CAP_EDGE",EDGE,{"disambiguationData":[OSD([subQ6])],"isStart":true})]})});}
            var Q21;
            Q21=makeQuery(id+"F17.boolean.opBoolean","INTERSECT",EDGE,{"derivedFrom":[makeQuery(id+"F13.boolean.opBoolean","MERGE",FACE,{"derivedFrom":[makeQuery(id+"F11.opExtrude","SWEPT_FACE",FACE,{"disambiguationData":[OSD([sQuery(id+"F10.wireOp",EDGE,"E25")])]}),makeQuery(id+"F13.opExtrude","SWEPT_FACE",FACE,{"disambiguationData":[OSD([sQuery(id+"F12.wireOp",EDGE,"E30")])]})]}),makeQuery(id+"F17.opExtrude","SWEPT_FACE",FACE,{"disambiguationData":[OSD([sQuery(id+"F16.wireOp",EDGE,"E42.right")])]})]});
            var Q22;
            Q22=makeQuery(id+"F17.boolean.opBoolean","INTERSECT",EDGE,{"derivedFrom":[makeQuery(id+"F13.boolean.opBoolean","MERGE",FACE,{"derivedFrom":[makeQuery(id+"F11.opExtrude","SWEPT_FACE",FACE,{"disambiguationData":[OSD([sQuery(id+"F10.wireOp",EDGE,"E25")])]}),makeQuery(id+"F13.opExtrude","SWEPT_FACE",FACE,{"disambiguationData":[OSD([sQuery(id+"F12.wireOp",EDGE,"E30")])]})]}),makeQuery(id+"F17.opExtrude","SWEPT_FACE",FACE,{"disambiguationData":[OSD([sQuery(id+"F16.wireOp",EDGE,"E42.left")])]})]});
            var Q23;
            {var subQ0=makeQuery(id+"F17.opExtrude","SWEPT_FACE",FACE,{"disambiguationData":[OSD([sQuery(id+"F16.wireOp",EDGE,"E45.MirrorCS")])]});var subQ1=sQuery(id+"F10.wireOp",EDGE,"E28.MirrorCS");Q23=makeQuery(id+"F24.opFillet","BLEND_EDGE",EDGE,{"blendedFrom":[makeQuery(id+"F17.boolean.opBoolean","SPLIT",EDGE,{"disambiguationData":[TD([subQ0])],"derivedFrom":makeQuery(id+"F11.opExtrude","CAP_EDGE",EDGE,{"disambiguationData":[OSD([subQ1])],"isStart":false})}),makeQuery(id+"F17.boolean.opBoolean","COPY",FACE,{"derivedFrom":subQ0})],"blendedInto":[makeQuery(id+"F17.boolean.opBoolean","COPY",FACE,{"derivedFrom":subQ0})]});}
            var Q24;
            {var subQ0=makeQuery(id+"F17.opExtrude","SWEPT_FACE",FACE,{"disambiguationData":[OSD([sQuery(id+"F16.wireOp",EDGE,"E43.MirrorCS")])]});var subQ1=sQuery(id+"F10.wireOp",EDGE,"E28.MirrorCS");Q24=makeQuery(id+"F24.opFillet","BLEND_EDGE",EDGE,{"blendedFrom":[makeQuery(id+"F17.boolean.opBoolean","SPLIT",EDGE,{"disambiguationData":[TD([subQ0])],"derivedFrom":makeQuery(id+"F11.opExtrude","CAP_EDGE",EDGE,{"disambiguationData":[OSD([subQ1])],"isStart":false})}),makeQuery(id+"F17.boolean.opBoolean","COPY",FACE,{"derivedFrom":subQ0})],"blendedInto":[makeQuery(id+"F17.boolean.opBoolean","COPY",FACE,{"derivedFrom":subQ0})]});}
            var Q25;
            Q25=makeQuery(id+"F17.boolean.opBoolean","INTERSECT",EDGE,{"derivedFrom":[makeQuery(id+"F11.opExtrude","CAP_FACE",FACE,{"disambiguationData":[OSD([sQuery(id+"F10.wireOp",EDGE,"E24"),sQuery(id+"F10.wireOp",EDGE,"E25"),sQuery(id+"F10.wireOp",EDGE,"E26"),sQuery(id+"F10.wireOp",EDGE,"E27.MirrorCS"),sQuery(id+"F10.wireOp",EDGE,"E28.MirrorCS"),sQuery(id+"F10.wireOp",EDGE,"E29.MirrorCS")])],"isStart":false}),makeQuery(id+"F17.opExtrude","SWEPT_FACE",FACE,{"disambiguationData":[OSD([sQuery(id+"F16.wireOp",EDGE,"E46.trimOffspring")])]})]});
            var Q26;
            Q26=makeQuery(id+"F17.boolean.opBoolean","INTERSECT",EDGE,{"derivedFrom":[makeQuery(id+"F11.opExtrude","CAP_FACE",FACE,{"disambiguationData":[OSD([sQuery(id+"F10.wireOp",EDGE,"E24"),sQuery(id+"F10.wireOp",EDGE,"E25"),sQuery(id+"F10.wireOp",EDGE,"E26"),sQuery(id+"F10.wireOp",EDGE,"E27.MirrorCS"),sQuery(id+"F10.wireOp",EDGE,"E28.MirrorCS"),sQuery(id+"F10.wireOp",EDGE,"E29.MirrorCS")])],"isStart":false}),makeQuery(id+"F17.opExtrude","SWEPT_FACE",FACE,{"disambiguationData":[OSD([sQuery(id+"F16.wireOp",EDGE,"E41")])]})]});
            var Q27;
            Q27=makeQuery(id+"F15.opExtrude","CAP_EDGE",EDGE,{"disambiguationData":[OSD([sQuery(id+"F14.wireOp",EDGE,"E38")])],"isStart":false});
            var Q28;
            Q28=makeQuery(id+"F15.opExtrude","CAP_EDGE",EDGE,{"disambiguationData":[OSD([sQuery(id+"F14.wireOp",EDGE,"E38")])],"isStart":true});
            var Q29;
            Q29=makeQuery(id+"F17.boolean.opBoolean","COPY",EDGE,{"derivedFrom":makeQuery(id+"F17.opExtrude","SWEPT_EDGE",EDGE,{"disambiguationData":[OSD([sQuery(id+"F16.wireOp",EDGE,"E41"),sQuery(id+"F16.wireOp",EDGE,"E45.MirrorCS")])]})});
            var Q30;
            Q30=makeQuery(id+"F17.boolean.opBoolean","COPY",EDGE,{"derivedFrom":makeQuery(id+"F17.opExtrude","SWEPT_EDGE",EDGE,{"disambiguationData":[OSD([sQuery(id+"F16.wireOp",EDGE,"E43.MirrorCS"),sQuery(id+"F16.wireOp",EDGE,"E46.trimOffspring")])]})});
            var Q31;
            Q31=makeQuery(id+"F17.boolean.opBoolean","COPY",EDGE,{"derivedFrom":makeQuery(id+"F17.opExtrude","SWEPT_EDGE",EDGE,{"disambiguationData":[OSD([sQuery(id+"F16.wireOp",EDGE,"E41"),sQuery(id+"F16.wireOp",EDGE,"E42.right")])]})});
            var Q32;
            Q32=makeQuery(id+"F17.boolean.opBoolean","COPY",EDGE,{"derivedFrom":makeQuery(id+"F17.opExtrude","SWEPT_EDGE",EDGE,{"disambiguationData":[OSD([sQuery(id+"F16.wireOp",EDGE,"E42.left"),sQuery(id+"F16.wireOp",EDGE,"E46.trimOffspring")])]})});
            fillet(context, id + "F25", {"entities" : qUnion([Q0, Q1, Q2, Q3, Q4, Q5, Q6, Q7, Q8, Q9, Q10, Q11, Q12, Q13, Q14, Q15, Q16, Q17, Q18, Q19, Q20, Q21, Q22, Q23, Q24, Q25, Q26, Q27, Q28, Q29, Q30, Q31, Q32]), "radius" : 1 * mm, "tangentPropagation" : true, "allowEdgeOverflow" : false});
        }
    });
